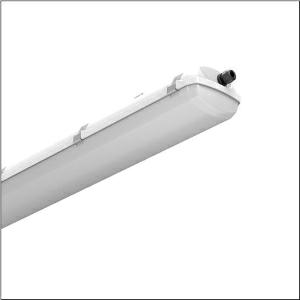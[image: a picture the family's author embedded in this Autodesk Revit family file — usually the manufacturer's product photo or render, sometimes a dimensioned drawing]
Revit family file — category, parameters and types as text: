
# Revit family: monsun_r__ex_51fxa27l440a_d3da
name_source: partatom
category: Lighting Fixtures
units: mm (PartAtom-declared; Revit-internal decimal feet)

## family parameters
Cut with Voids When Loaded = No
Host = Face
Light Source = No
Part Type = Normal
Room Calculation Point = No
Round Connector Dimension = Use Diameter
Shared = No

## types (1)
- Monsun® Ex (1 x LED, 4650 lm, 30 W, 4000K)
    Apparent Load = 30 VA
    CIE Flux Codes = 46 76 94 98 100
    Color Rendering = 80
    Color Temperature = 4000K
    Default Elevation = 1800 mm
    Description = Monsun® Ex, damp-proof luminaire, primary optical cover: cover, of PC, UV-stabilised, opal, light emission: direct distribution, primary light characteristic: symmetric, installation type: surface-mounted, LED, rated luminous flux: 4.650lm, luminous efficacy: 155lm/W, light colour: 840, colour temperature: 4000K, control gear: ECG, with terminal, 3-pole, max. 2.5mm², through-wiring: 5x 2.5mm², mains connection: 220..250V, AC, 50/60Hz, rated input power: 30W, housing, of PC, light grey (RAL 7035), incl. 1x Ex cable gland M20 for cable diameter 7..12mm with sealing, incl. 1x Ex locking screw M20 with sealing, length: 1.280mm, width: 155mm, height: 105mm, clip for enclosure, of stainless steel, protection rating (complete): IP66, insulation class (complete): insulation class I (protective earthing), certification: CE, explosion class: zone 1,21 II 2G Ex eb mb op is IIC T4 Gb, II 2D Ex tb op is IIIC T67°C Db, impact resistance: IK10, permissible operating ambient temperature: -20..+40°C, contact your sales advisor before using the luminaires in applications with unclear chemical exposure, large temperature fluctuations or condensation-forming humidity, packaging unit: 1 piece
    Height = 105 mm
    Lamp = 1 x LED
    Lamp Light Flux = 4650 lm
    Lamp Power = 30 W
    Lamp count = 1
    Length = 1280 mm
    Luminous efficacy = 155 lm/W
    Manufacturer = Siteco
    ModVariant = No
    Model = 51FXA27L440A
    Mounting Place = Ceiling
    Mounting Type = Surface mounted
    Number of Poles = 1
    OnlyDefault = Yes
    Power Factor = 1
    Product Name = Monsun® Ex
    Product group = damp-proof luminaire
    ProductGroupID = 300
    Protection Class = Protection class I
    Protection Degree = IP 66
    RLX_Detail_Level = 1
    RLX_Emergency_Light_Flux = 0 lm
    RLX_Emergency_Type = 0
    RLX_Emergency_Type_DB = No
    RlxData = <blob elided: 41429 chars, md5=c2eb3c15>
    Socket = socket
    Standby Power = 0 W
    System Light Flux = 4650 lm
    System Power = 30 W
    Type Comments = Product without accessories
    Type Image = l_1258882.jpg
    URL = http://relux.com
    VarID = ---
    Voltage = 0 V
    Weight = 0.00 kg
    Width = 155 mm

## geometry (parser evidence)
native form markers: Blend x4, Sweep x11
no freeform markers — native parametric forms only
